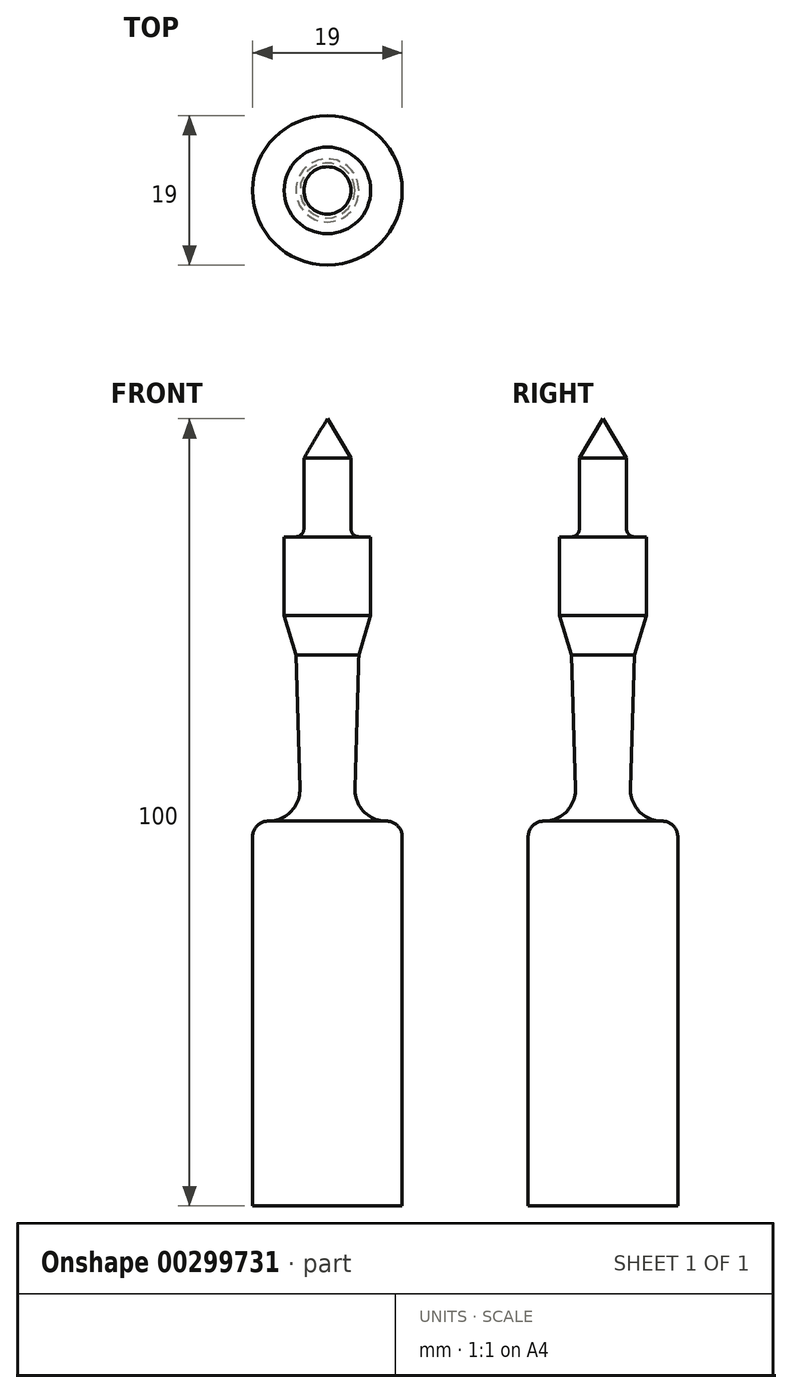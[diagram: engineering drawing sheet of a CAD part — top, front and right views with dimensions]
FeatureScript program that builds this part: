
annotation { "Feature Type Name" : "Feature", "Feature Type Description" : "" }
export const myFeature = defineFeature(function(context is Context, id is Id, definition is map)
    precondition{}
    {
        {
            var Q0;
            Q0=qCreatedBy(makeId("Front.planeOp"),FACE);
            var sketch = newSketch(context, id + "F0", { "sketchPlane" : qUnion([Q0])});
            skLineSegment(sketch, "E0", {"start": v(0, 0) * mm, "end": v(0, -100) * mm});
            skLineSegment(sketch, "E1", {"start": v(3, -5) * mm, "end": v(3, -14) * mm});
            skArc(sketch, "E2", {"start": v(3, -14) * mm, "mid": v(3.3, -14.7) * mm, "end": v(4, -15) * mm});
            skLineSegment(sketch, "E3", {"start": v(4, -15) * mm, "end": v(5.5, -15) * mm});
            skLineSegment(sketch, "E4", {"start": v(5.5, -15) * mm, "end": v(5.5, -25) * mm});
            skLineSegment(sketch, "E5", {"start": v(5.5, -25) * mm, "end": v(4, -30) * mm});
            skLineSegment(sketch, "E6", {"start": v(4, -30) * mm, "end": v(3.5, -47) * mm});
            skArc(sketch, "E7", {"start": v(3.5, -47) * mm, "mid": v(4.63, -49.9) * mm, "end": v(7.5, -51.12) * mm});
            skArc(sketch, "E8", {"start": v(9.5, -53.12) * mm, "mid": v(8.91, -51.7) * mm, "end": v(7.5, -51.12) * mm});
            skLineSegment(sketch, "E9", {"start": v(9.5, -53.12) * mm, "end": v(9.5, -100) * mm});
            skLineSegment(sketch, "E10", {"start": v(9.5, -100) * mm, "end": v(0, -100) * mm});
            skLineSegment(sketch, "E11", {"start": v(0, 0) * mm, "end": v(3, -5) * mm});
            skSolve(sketch);
        }
        {
            var Q0;
            Q0 = qSketchRegion(id + "F0", true);
            var Q1;
            Q1 = qConstructionFilter(qBodyType(qCreatedBy(id + "F0" ,EDGE), BodyType.WIRE), ConstructionObject.NO);
            var Q2;
            Q2=sQuery(id+"F0.wireOp",EDGE,"E0");
            revolve(context, id + "F1", {"entities" : qUnion([Q0]), "surfaceEntities" : qUnion([Q1]), "axis" : qUnion([Q2]), "revolveType" : RevolveType.FULL});
        }
    });
